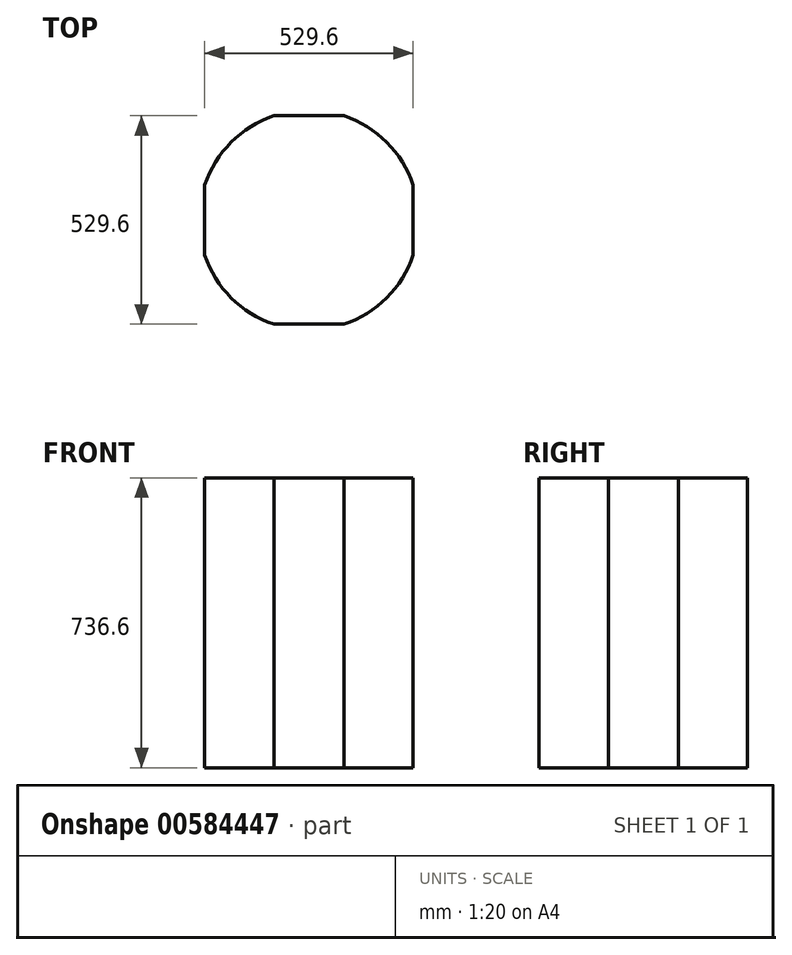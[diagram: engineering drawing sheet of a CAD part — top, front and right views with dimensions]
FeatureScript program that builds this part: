
annotation { "Feature Type Name" : "Feature", "Feature Type Description" : "" }
export const myFeature = defineFeature(function(context is Context, id is Id, definition is map)
    precondition{}
    {
        {
            var Q0;
            Q0=qCreatedBy(makeId("Top.planeOp"),FACE);
            var sketch = newSketch(context, id + "F0", { "sketchPlane" : qUnion([Q0])});
            skCircle(sketch, "E0", {"center": v(0, 0) * mm, "radius": 279.4 * mm});
            skSolve(sketch);
        }
        {
            var Q0;
            Q0=qSketchRegion(id+"F0",true);
            extrude(context, id + "F1", {"entities" : qUnion([Q0]), "depth" : 736.6 * mm, "offsetDistance" : 25.4 * mm});
        }
        {
            var Q0;
            Q0=qCreatedBy(makeId("Top.planeOp"),FACE);
            var sketch = newSketch(context, id + "F2", { "sketchPlane" : qUnion([Q0])});
            skLineSegment(sketch, "E1.bottom", {"start": v(-97.5, 264.8) * mm, "end": v(98.26, 264.8) * mm});
            skLineSegment(sketch, "E1.top", {"start": v(-97.5, 290.2) * mm, "end": v(98.26, 290.2) * mm});
            skLineSegment(sketch, "E1.left", {"start": v(-97.5, 264.8) * mm, "end": v(-97.5, 290.2) * mm});
            skLineSegment(sketch, "E1.right", {"start": v(98.26, 264.8) * mm, "end": v(98.26, 290.2) * mm});
            skLineSegment(sketch, "E2.1.0", {"start": v(-264.8, -97.5) * mm, "end": v(-264.8, 98.26) * mm});
            skLineSegment(sketch, "E2.1.1", {"start": v(-290.2, -97.5) * mm, "end": v(-290.2, 98.26) * mm});
            skLineSegment(sketch, "E2.1.2", {"start": v(-264.8, 98.26) * mm, "end": v(-290.2, 98.26) * mm});
            skLineSegment(sketch, "E2.1.3", {"start": v(-264.8, -97.5) * mm, "end": v(-290.2, -97.5) * mm});
            skLineSegment(sketch, "E2.2.0", {"start": v(97.5, -264.8) * mm, "end": v(-98.26, -264.8) * mm});
            skLineSegment(sketch, "E2.2.1", {"start": v(97.5, -290.2) * mm, "end": v(-98.26, -290.2) * mm});
            skLineSegment(sketch, "E2.2.2", {"start": v(-98.26, -264.8) * mm, "end": v(-98.26, -290.2) * mm});
            skLineSegment(sketch, "E2.2.3", {"start": v(97.5, -264.8) * mm, "end": v(97.5, -290.2) * mm});
            skLineSegment(sketch, "E2.3.0", {"start": v(264.8, 97.5) * mm, "end": v(264.8, -98.26) * mm});
            skLineSegment(sketch, "E2.3.1", {"start": v(290.2, 97.5) * mm, "end": v(290.2, -98.26) * mm});
            skLineSegment(sketch, "E2.3.2", {"start": v(264.8, -98.26) * mm, "end": v(290.2, -98.26) * mm});
            skLineSegment(sketch, "E2.3.3", {"start": v(264.8, 97.5) * mm, "end": v(290.2, 97.5) * mm});
            skPoint(sketch, "E2.center", {"position": v(0, 0) * mm});
            skSolve(sketch);
        }
        {
            var Q0;
            Q0=qSketchRegion(id+"F2",true);
            extrude(context, id + "F3", {"entities" : qUnion([Q0]), "operationType" : NewBodyOperationType.REMOVE, "depth" : 1010.92 * mm, "offsetDistance" : 25.4 * mm});
        }
    });
